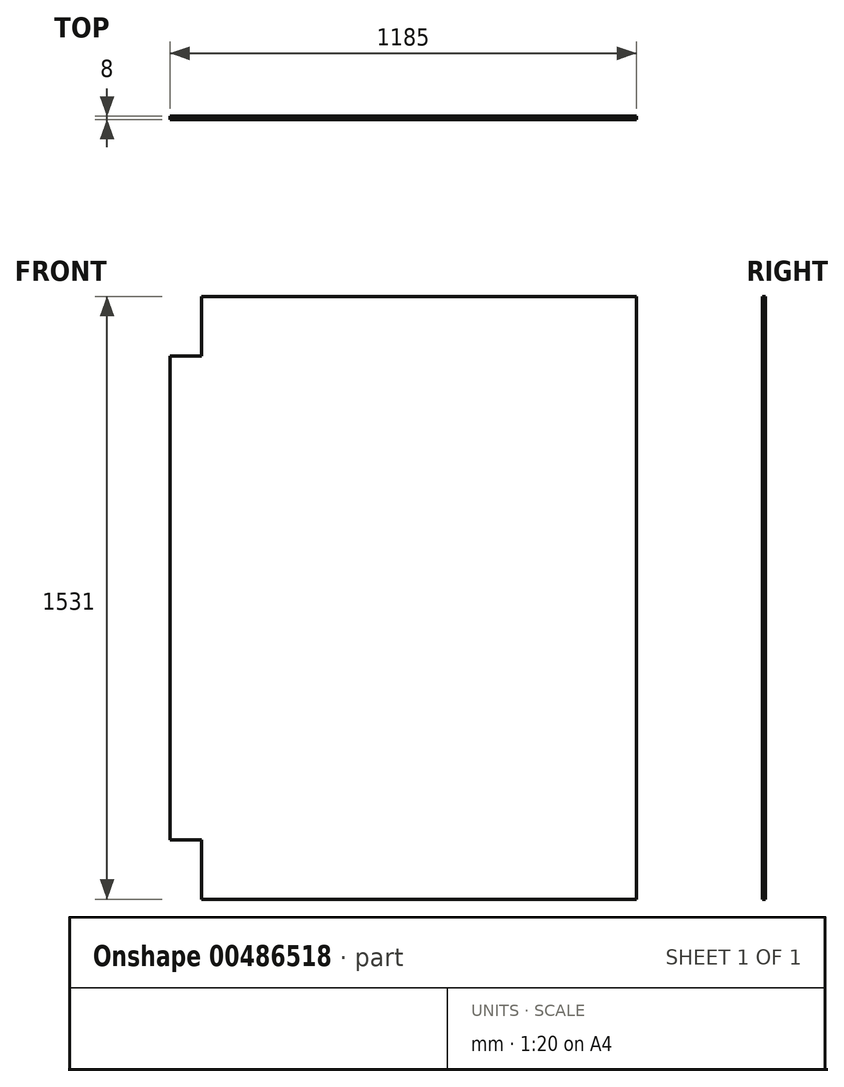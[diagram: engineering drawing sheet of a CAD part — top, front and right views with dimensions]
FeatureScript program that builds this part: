
annotation { "Feature Type Name" : "Feature", "Feature Type Description" : "" }
export const myFeature = defineFeature(function(context is Context, id is Id, definition is map)
    precondition{}
    {
        {
            var Q0;
            Q0=qCreatedBy(makeId("Front.planeOp"),FACE);
            var sketch = newSketch(context, id + "F0", { "sketchPlane" : qUnion([Q0])});
            skLineSegment(sketch, "E0.bottom", {"start": v(-641.52, 1109.27) * mm, "end": v(463.48, 1109.27) * mm});
            skLineSegment(sketch, "E0.top", {"start": v(-641.52, -421.73) * mm, "end": v(463.48, -421.73) * mm});
            skLineSegment(sketch, "E0.left", {"start": v(-641.52, 1109.27) * mm, "end": v(-641.52, -421.73) * mm});
            skLineSegment(sketch, "E0.right", {"start": v(463.48, 1109.27) * mm, "end": v(463.48, -421.73) * mm});
            skLineSegment(sketch, "E1", {"start": v(-641.52, 958.77) * mm, "end": v(-721.52, 958.77) * mm});
            skLineSegment(sketch, "E2", {"start": v(-641.52, -271.23) * mm, "end": v(-721.52, -271.23) * mm});
            skLineSegment(sketch, "E3", {"start": v(-721.52, 958.77) * mm, "end": v(-721.52, -271.23) * mm});
            skSolve(sketch);
        }
        {
            var Q0;
            Q0 = qSketchRegion(id + "F0", true);
            extrude(context, id + "F1", {"entities" : qUnion([Q0]), "depth" : 8 * mm, "offsetDistance" : 25 * mm});
        }
    });
